# Revit family: Toilet_Seat-Elongated_Closed_Front-KOHLER-MODERN_LIFE-K-77168IN
name_source: partatom
category: Specialty Equipment
revit_build: Autodesk Revit 2017 (Build: 20160225_1515(x64)
units: mm (PartAtom-declared; Revit-internal decimal feet)

## family parameters
Cut with Voids When Loaded = No
Host = Face
OmniClass Number = 23.31.25.00
Part Type = Normal
Room Calculation Point = No
Round Connector Dimension = Use Diameter
Shared = No

## types (2) — shared parameters
ADA Compliant = No
Assembly Code = C1030200
Date Modified = 12/22/2020
Default Elevation = 0"
Description = SS WH SEAT
Finish = Kohler-Plastic-0-White
Height = 1 3/4"
Length = 17 3/8"
Manufacturer = KOHLER Co.
Master Format 2014 = 10 28 00
Master Format 2014 Name = Toilet, Bath, and Laundry Accessories
Material = Plastic
Product Name = MODERN LIFE
URL = https://www.kohler.co.in
WaterSense Certified = No
Width = 14 3/16"

## per-type parameters (varying)
| type | Model | Product Page URL | Type |
| SS, 0- White | K-77168IN-SS-0 | https://www.kohler.co.in | 1 |
| UF, 0- White | K-77168IN-UF-0 |  | 2 |

## geometry (parser evidence)
native form markers: Sweep x6
no freeform markers — native parametric forms only
